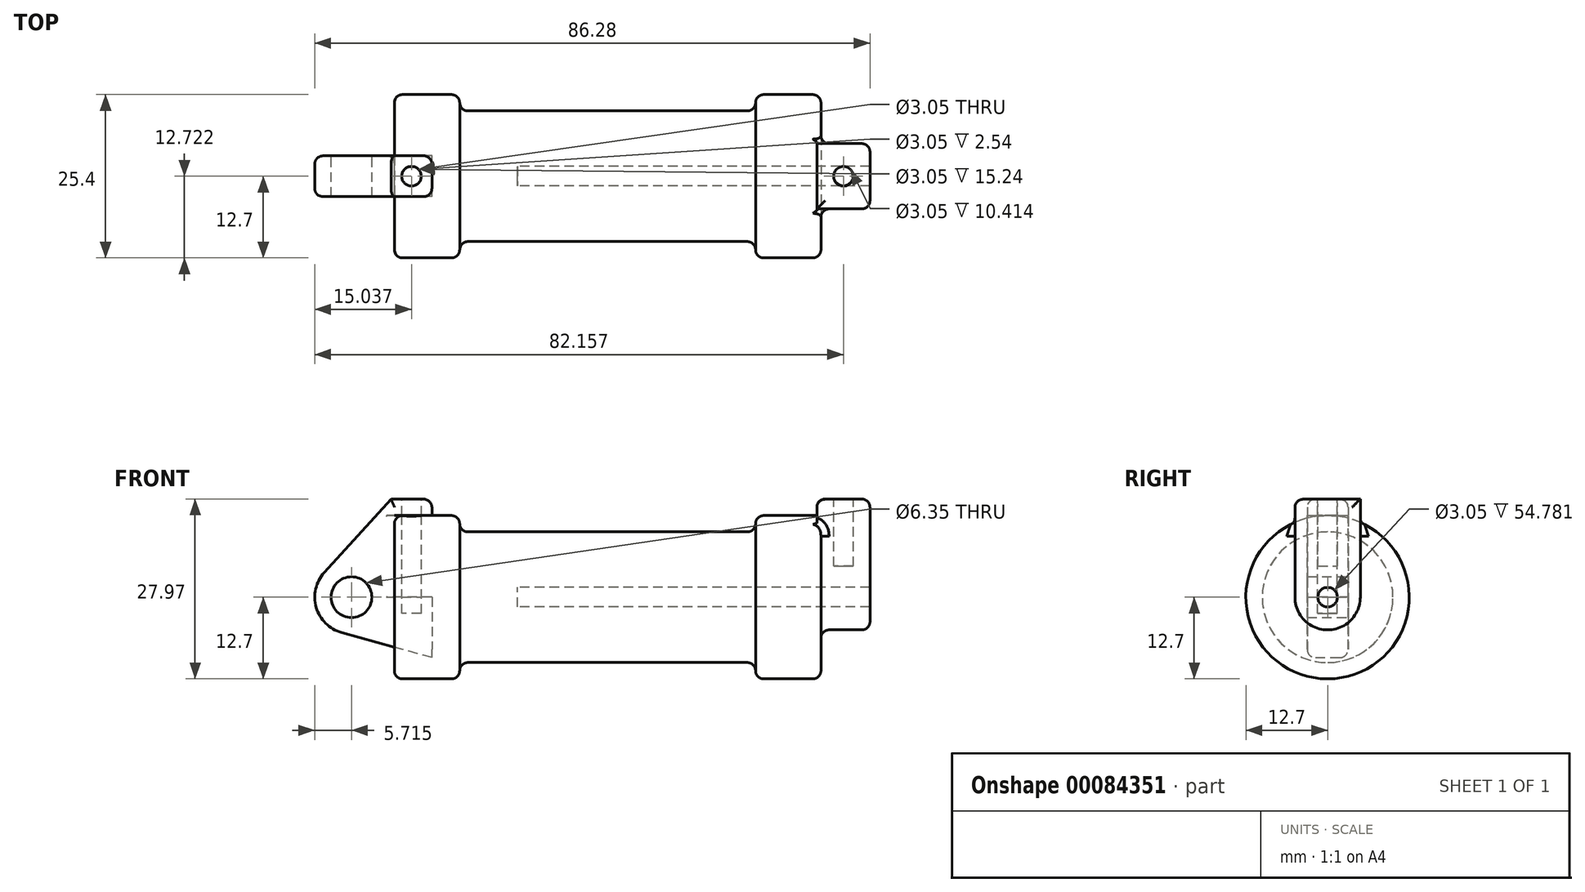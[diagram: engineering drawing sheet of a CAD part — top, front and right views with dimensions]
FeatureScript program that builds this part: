
annotation { "Feature Type Name" : "Feature", "Feature Type Description" : "" }
export const myFeature = defineFeature(function(context is Context, id is Id, definition is map)
    precondition{}
    {
        {
            var Q0;
            Q0=qCreatedBy(makeId("Front.planeOp"),FACE);
            var sketch = newSketch(context, id + "F0", { "sketchPlane" : qUnion([Q0])});
            skLineSegment(sketch, "E0", {"start": v(0, 0) * mm, "end": v(0, 12.7) * mm});
            skLineSegment(sketch, "E1", {"start": v(0, 12.7) * mm, "end": v(10.16, 12.7) * mm});
            skLineSegment(sketch, "E2", {"start": v(10.16, 12.7) * mm, "end": v(10.16, 10.16) * mm});
            skLineSegment(sketch, "E3", {"start": v(10.16, 10.16) * mm, "end": v(56.13, 10.16) * mm});
            skLineSegment(sketch, "E4", {"start": v(56.13, 10.16) * mm, "end": v(56.13, 12.7) * mm});
            skLineSegment(sketch, "E5", {"start": v(56.13, 12.7) * mm, "end": v(66.3, 12.7) * mm});
            skLineSegment(sketch, "E6", {"start": v(66.3, 12.7) * mm, "end": v(66.3, 0) * mm});
            skLineSegment(sketch, "E7", {"start": v(66.3, 0) * mm, "end": v(0, 0) * mm});
            skLineSegment(sketch, "E8", {"start": v(5.84, 15.24) * mm, "end": v(-0.5, 15.24) * mm});
            skLineSegment(sketch, "E9", {"start": v(-0.5, 15.24) * mm, "end": v(-10.88, 3.85) * mm});
            skLineSegment(sketch, "E10", {"start": v(0, 0) * mm, "end": v(-6.65, 0) * mm});
            skCircle(sketch, "E11", {"center": v(-6.65, 0) * mm, "radius": 5.72 * mm});
            skCircle(sketch, "E12", {"center": v(-6.65, 0) * mm, "radius": 3.18 * mm});
            skLineSegment(sketch, "E13", {"start": v(5.84, 15.24) * mm, "end": v(5.84, -9.4) * mm});
            skLineSegment(sketch, "E14", {"start": v(5.84, -9.4) * mm, "end": v(-8.18, -5.5) * mm});
            skSolve(sketch);
        }
        {
            var Q0;
            {var subQ0=sQuery(id+"F0.wireOp",EDGE,"E2");Q0=makeQuery(id+"F0.imprint","IMPRINT",FACE,{"disambiguationData":[TD([[makeQuery(id+"F0.imprint","IMPRINT",EDGE,{"derivedFrom":subQ0}),-1.0]])]});}
            var Q1;
            {var subQ0=sQuery(id+"F0.wireOp",EDGE,"E0");Q1=makeQuery(id+"F0.imprint","IMPRINT",FACE,{"disambiguationData":[TD([[makeQuery(id+"F0.imprint","IMPRINT",EDGE,{"derivedFrom":subQ0}),-1.0]])]});}
            var Q2;
            Q2=sQuery(id+"F0.wireOp",EDGE,"E7");
            revolve(context, id + "F1", {"entities" : qUnion([Q0, Q1]), "axis" : qUnion([Q2]), "revolveType" : RevolveType.FULL});
        }
        {
            var Q0;
            {var subQ3=sQuery(id+"F0.wireOp",EDGE,"E0");Q0=makeQuery(id+"F0.imprint","IMPRINT",FACE,{"disambiguationData":[TD([[makeQuery(id+"F0.imprint","IMPRINT",EDGE,{"derivedFrom":subQ3}),1.0]])]});}
            var Q1;
            {var subQ4=sQuery(id+"F0.wireOp",EDGE,"E12");Q1=makeQuery(id+"F0.imprint","IMPRINT",FACE,{"disambiguationData":[TD([[makeQuery(id+"F0.imprint","IMPRINT",EDGE,{"derivedFrom":subQ4}),-1.0]])]});}
            var Q2;
            {var subQ0=sQuery(id+"F0.wireOp",EDGE,"E14");Q2=makeQuery(id+"F0.imprint","IMPRINT",FACE,{"disambiguationData":[TD([[makeQuery(id+"F0.imprint","IMPRINT",EDGE,{"derivedFrom":subQ0}),-1.0]])]});}
            extrude(context, id + "F2", {"entities" : qUnion([Q0, Q1, Q2]), "endBound" : BoundingType.SYMMETRIC, "depth" : 6.35 * mm});
        }
        {
            var Q0;
            Q0=makeQuery(id+"F1.opRevolve","SWEPT_FACE",FACE,{"disambiguationData":[OSD([sQuery(id+"F0.wireOp",EDGE,"E6")])]});
            var sketch = newSketch(context, id + "F3", { "sketchPlane" : qUnion([Q0])});
            skCircle(sketch, "E15", {"center": v(0, 0) * mm, "radius": 1.52 * mm});
            skCircle(sketch, "E16", {"center": v(0, 0) * mm, "radius": 5.08 * mm});
            skLineSegment(sketch, "E17", {"start": v(-5.08, 0) * mm, "end": v(-5.08, 15.23) * mm});
            skLineSegment(sketch, "E18", {"start": v(5.08, 0.03) * mm, "end": v(5.08, 15.27) * mm});
            skLineSegment(sketch, "E19", {"start": v(-5.08, 15.23) * mm, "end": v(5.1, 15.27) * mm});
            skSolve(sketch);
        }
        {
            var Q0;
            {var subQ0=sQuery(id+"F3.wireOp",EDGE,"E17");var subQ1=sQuery(id+"F3.wireOp",EDGE,"E16");var subQ2=makeQuery(id+"F3.imprint","INTERSECT",VERTEX,{"derivedFrom":[subQ1,subQ0]});Q0=makeQuery(id+"F3.imprint","IMPRINT",FACE,{"disambiguationData":[TD([[makeQuery(id+"F3.imprint","IMPRINT",EDGE,{"disambiguationData":[TD([[subQ2,1.0]])],"derivedFrom":subQ1}),-1.0]])]});}
            var Q1;
            {var subQ0=sQuery(id+"F3.wireOp",EDGE,"E19");var subQ1=sQuery(id+"F3.wireOp",EDGE,"E17");var subQ2=makeQuery(id+"F3.imprint","INTERSECT",VERTEX,{"derivedFrom":[subQ1,subQ0]});Q1=makeQuery(id+"F3.imprint","IMPRINT",FACE,{"disambiguationData":[TD([[makeQuery(id+"F3.imprint","IMPRINT",EDGE,{"disambiguationData":[TD([[subQ2,-1.0]])],"derivedFrom":subQ0}),-1.0]])]});}
            var Q2;
            Q2=makeQuery(id+"F3.imprint","IMPRINT",FACE,{"disambiguationData":[TD([[makeQuery(id+"F3.imprint","IMPRINT",EDGE,{"derivedFrom":sQuery(id+"F3.wireOp",EDGE,"E15")}),-1.0]])]});
            extrude(context, id + "F4", {"entities" : qUnion([Q0, Q1, Q2]), "operationType" : NewBodyOperationType.ADD, "depth" : 7.62 * mm});
        }
        {
            var Q0;
            Q0=makeQuery(id+"F4.opExtrude","CAP_FACE",FACE,{"disambiguationData":[OSD([sQuery(id+"F3.wireOp",EDGE,"E15"),sQuery(id+"F3.wireOp",EDGE,"E16"),sQuery(id+"F3.wireOp",EDGE,"E17"),sQuery(id+"F3.wireOp",EDGE,"E18"),sQuery(id+"F3.wireOp",EDGE,"E19")])],"isStart":true});
            extrude(context, id + "F5", {"entities" : qUnion([Q0]), "operationType" : NewBodyOperationType.ADD, "endBound" : BoundingType.SYMMETRIC, "depth" : 1.27 * mm});
        }
        {
            var Q0;
            Q0=makeQuery(id+"F4.boolean.opBoolean","SPLIT",FACE,{"disambiguationData":[TD([makeQuery(id+"F4.opExtrude","SWEPT_FACE",FACE,{"disambiguationData":[OSD([sQuery(id+"F3.wireOp",EDGE,"E15")])]})])],"derivedFrom":makeQuery(id+"F1.opRevolve","SWEPT_FACE",FACE,{"disambiguationData":[OSD([sQuery(id+"F0.wireOp",EDGE,"E6")])]})});
            extrude(context, id + "F6", {"entities" : qUnion([Q0]), "operationType" : NewBodyOperationType.REMOVE, "oppositeDirection" : true, "depth" : 47.16 * mm});
        }
        {
            var Q0;
            {var subQ0=sQuery(id+"F3.wireOp",EDGE,"E19");Q0=makeQuery(id+"F5.boolean.opBoolean","MERGE",FACE,{"derivedFrom":[makeQuery(id+"F4.opExtrude","SWEPT_FACE",FACE,{"disambiguationData":[OSD([subQ0])]}),makeQuery(id+"F5.opExtrude","SWEPT_FACE",FACE,{"disambiguationData":[OSD([subQ0])]})]});}
            var sketch = newSketch(context, id + "F7", { "sketchPlane" : qUnion([Q0])});
            skCircle(sketch, "E20", {"center": v(69.79, 0.06) * mm, "radius": 1.52 * mm});
            skSolve(sketch);
        }
        {
            var Q0;
            Q0=makeQuery(id+"F2.opExtrude","SWEPT_FACE",FACE,{"disambiguationData":[OSD([sQuery(id+"F0.wireOp",EDGE,"E8")])]});
            var sketch = newSketch(context, id + "F8", { "sketchPlane" : qUnion([Q0])});
            skCircle(sketch, "E21", {"center": v(2.67, 0) * mm, "radius": 1.52 * mm});
            skSolve(sketch);
        }
        {
            var Q0;
            Q0=makeQuery(id+"F8.imprint","IMPRINT",FACE,{"disambiguationData":[TD([[makeQuery(id+"F8.imprint","IMPRINT",EDGE,{"derivedFrom":sQuery(id+"F8.wireOp",EDGE,"E21")}),1.0]])]});
            var Q1;
            Q1=sQuery(id+"F8.wireOp",EDGE,"E21");
            extrude(context, id + "F9", {"entities" : qUnion([Q0]), "operationType" : NewBodyOperationType.REMOVE, "surfaceEntities" : qUnion([Q1]), "oppositeDirection" : true, "depth" : 17.78 * mm});
        }
        {
            var Q0;
            Q0=makeQuery(id+"F7.imprint","IMPRINT",FACE,{"disambiguationData":[TD([[makeQuery(id+"F7.imprint","IMPRINT",EDGE,{"derivedFrom":sQuery(id+"F7.wireOp",EDGE,"E20")}),1.0]])]});
            var Q1;
            Q1=sQuery(id+"F7.wireOp",EDGE,"E20");
            extrude(context, id + "F10", {"entities" : qUnion([Q0]), "operationType" : NewBodyOperationType.REMOVE, "surfaceEntities" : qUnion([Q1]), "oppositeDirection" : true, "depth" : 10.4 * mm});
        }
        {
            var Q0;
            Q0=makeQuery(id+"F1.opRevolve","SWEPT_EDGE",EDGE,{"disambiguationData":[OSD([sQuery(id+"F0.wireOp",EDGE,"E1"),sQuery(id+"F0.wireOp",EDGE,"E2")])]});
            var Q1;
            Q1=makeQuery(id+"F1.opRevolve","SWEPT_EDGE",EDGE,{"disambiguationData":[OSD([sQuery(id+"F0.wireOp",EDGE,"E2"),sQuery(id+"F0.wireOp",EDGE,"E3")])]});
            var Q2;
            Q2=makeQuery(id+"F1.opRevolve","SWEPT_EDGE",EDGE,{"disambiguationData":[OSD([sQuery(id+"F0.wireOp",EDGE,"E4"),sQuery(id+"F0.wireOp",EDGE,"E5")])]});
            var Q3;
            Q3=makeQuery(id+"F1.opRevolve","SWEPT_EDGE",EDGE,{"disambiguationData":[OSD([sQuery(id+"F0.wireOp",EDGE,"E3"),sQuery(id+"F0.wireOp",EDGE,"E4")])]});
            var Q4;
            Q4=makeQuery(id+"F4.boolean.opBoolean","SPLIT",EDGE,{"disambiguationData":[OD(1.0)],"derivedFrom":makeQuery(id+"F1.opRevolve","SWEPT_EDGE",EDGE,{"disambiguationData":[OSD([sQuery(id+"F0.wireOp",EDGE,"E5"),sQuery(id+"F0.wireOp",EDGE,"E6")])]})});
            var Q5;
            Q5=makeQuery(id+"F1.opRevolve","SWEPT_EDGE",EDGE,{"disambiguationData":[OSD([sQuery(id+"F0.wireOp",EDGE,"E0"),sQuery(id+"F0.wireOp",EDGE,"E1")])]});
            fillet(context, id + "F11", {"entities" : qUnion([Q0, Q1, Q2, Q3, Q4, Q5]), "radius" : 1.27 * mm, "tangentPropagation" : true, "allowEdgeOverflow" : false});
        }
        {
            var Q0;
            Q0=makeQuery(id+"F2.opExtrude","CAP_EDGE",EDGE,{"disambiguationData":[OSD([sQuery(id+"F0.wireOp",EDGE,"E0")])],"isStart":true});
            var Q1;
            Q1=makeQuery(id+"F4.opExtrude","CAP_EDGE",EDGE,{"disambiguationData":[OSD([sQuery(id+"F3.wireOp",EDGE,"E17")])],"isStart":false});
            var Q2;
            Q2=makeQuery(id+"F4.opExtrude","CAP_EDGE",EDGE,{"disambiguationData":[OSD([sQuery(id+"F3.wireOp",EDGE,"E19")])],"isStart":false});
            var Q3;
            Q3=makeQuery(id+"F4.opExtrude","CAP_EDGE",EDGE,{"disambiguationData":[OSD([sQuery(id+"F3.wireOp",EDGE,"E16")])],"isStart":false});
            var Q4;
            Q4=makeQuery(id+"F4.opExtrude","CAP_EDGE",EDGE,{"disambiguationData":[OSD([sQuery(id+"F3.wireOp",EDGE,"E18")])],"isStart":false});
            var Q5;
            Q5=makeQuery(id+"F4.opExtrude","CAP_EDGE",EDGE,{"disambiguationData":[OSD([sQuery(id+"F3.wireOp",EDGE,"E16")])],"isStart":true});
            var Q6;
            {var subQ0=sQuery(id+"F3.wireOp",EDGE,"E16");var subQ1=sQuery(id+"F3.wireOp",EDGE,"E18");Q6=makeQuery(id+"F4.boolean.opBoolean","SPLIT",EDGE,{"disambiguationData":[TD([makeQuery(id+"F4.opExtrude","SWEPT_FACE",FACE,{"disambiguationData":[OSD([subQ0])]})])],"derivedFrom":makeQuery(id+"F4.opExtrude","CAP_EDGE",EDGE,{"disambiguationData":[OSD([subQ1])],"isStart":true})});}
            var Q7;
            {var subQ0=sQuery(id+"F3.wireOp",EDGE,"E19");var subQ1=sQuery(id+"F3.wireOp",EDGE,"E18");Q7=makeQuery(id+"F5.boolean.opBoolean","MERGE",EDGE,{"derivedFrom":[makeQuery(id+"F4.opExtrude","SWEPT_EDGE",EDGE,{"disambiguationData":[OSD([subQ1,subQ0])]}),makeQuery(id+"F5.opExtrude","SWEPT_EDGE",EDGE,{"disambiguationData":[OSD([subQ1,subQ0])]})]});}
            var Q8;
            {var subQ0=sQuery(id+"F3.wireOp",EDGE,"E16");var subQ1=sQuery(id+"F3.wireOp",EDGE,"E17");Q8=makeQuery(id+"F4.boolean.opBoolean","SPLIT",EDGE,{"disambiguationData":[TD([makeQuery(id+"F4.opExtrude","SWEPT_FACE",FACE,{"disambiguationData":[OSD([subQ0])]})])],"derivedFrom":makeQuery(id+"F4.opExtrude","CAP_EDGE",EDGE,{"disambiguationData":[OSD([subQ1])],"isStart":true})});}
            var Q9;
            Q9=makeQuery(id+"F5.opExtrude","CAP_EDGE",EDGE,{"disambiguationData":[OSD([sQuery(id+"F3.wireOp",EDGE,"E19")])],"isStart":false});
            var Q10;
            {var subQ0=sQuery(id+"F3.wireOp",EDGE,"E17");Q10=makeQuery(id+"F11.opFillet","BLEND_EDGE",EDGE,{"blendedFrom":[makeQuery(id+"F4.boolean.opBoolean","SPLIT",EDGE,{"disambiguationData":[OD(1.0)],"derivedFrom":makeQuery(id+"F1.opRevolve","SWEPT_EDGE",EDGE,{"disambiguationData":[OSD([sQuery(id+"F0.wireOp",EDGE,"E5"),sQuery(id+"F0.wireOp",EDGE,"E6")])]})}),makeQuery(id+"F5.boolean.opBoolean","MERGE",FACE,{"derivedFrom":[makeQuery(id+"F4.opExtrude","SWEPT_FACE",FACE,{"disambiguationData":[OSD([subQ0])]}),makeQuery(id+"F5.opExtrude","SWEPT_FACE",FACE,{"disambiguationData":[OSD([subQ0])]})]})],"blendedInto":[makeQuery(id+"F5.boolean.opBoolean","MERGE",FACE,{"derivedFrom":[makeQuery(id+"F4.opExtrude","SWEPT_FACE",FACE,{"disambiguationData":[OSD([subQ0])]}),makeQuery(id+"F5.opExtrude","SWEPT_FACE",FACE,{"disambiguationData":[OSD([subQ0])]})]})]});}
            var Q11;
            {var subQ0=sQuery(id+"F3.wireOp",EDGE,"E18");Q11=makeQuery(id+"F11.opFillet","BLEND_EDGE",EDGE,{"blendedFrom":[makeQuery(id+"F4.boolean.opBoolean","SPLIT",EDGE,{"disambiguationData":[OD(1.0)],"derivedFrom":makeQuery(id+"F1.opRevolve","SWEPT_EDGE",EDGE,{"disambiguationData":[OSD([sQuery(id+"F0.wireOp",EDGE,"E5"),sQuery(id+"F0.wireOp",EDGE,"E6")])]})}),makeQuery(id+"F5.boolean.opBoolean","MERGE",FACE,{"derivedFrom":[makeQuery(id+"F4.opExtrude","SWEPT_FACE",FACE,{"disambiguationData":[OSD([subQ0])]}),makeQuery(id+"F5.opExtrude","SWEPT_FACE",FACE,{"disambiguationData":[OSD([subQ0])]})]})],"blendedInto":[makeQuery(id+"F5.boolean.opBoolean","MERGE",FACE,{"derivedFrom":[makeQuery(id+"F4.opExtrude","SWEPT_FACE",FACE,{"disambiguationData":[OSD([subQ0])]}),makeQuery(id+"F5.opExtrude","SWEPT_FACE",FACE,{"disambiguationData":[OSD([subQ0])]})]})]});}
            var Q12;
            {var subQ0=sQuery(id+"F3.wireOp",EDGE,"E19");var subQ1=sQuery(id+"F3.wireOp",EDGE,"E17");Q12=makeQuery(id+"F5.boolean.opBoolean","MERGE",EDGE,{"derivedFrom":[makeQuery(id+"F4.opExtrude","SWEPT_EDGE",EDGE,{"disambiguationData":[OSD([subQ1,subQ0])]}),makeQuery(id+"F5.opExtrude","SWEPT_EDGE",EDGE,{"disambiguationData":[OSD([subQ1,subQ0])]})]});}
            var Q13;
            Q13=makeQuery(id+"F5.opExtrude","CAP_EDGE",EDGE,{"disambiguationData":[OSD([sQuery(id+"F0.wireOp",EDGE,"E5"),sQuery(id+"F0.wireOp",EDGE,"E6")])],"isStart":false});
            var Q14;
            Q14=makeQuery(id+"F2.opExtrude","CAP_EDGE",EDGE,{"disambiguationData":[OSD([sQuery(id+"F0.wireOp",EDGE,"E9")])],"isStart":false});
            var Q15;
            Q15=makeQuery(id+"F2.opExtrude","CAP_EDGE",EDGE,{"disambiguationData":[OSD([sQuery(id+"F0.wireOp",EDGE,"E8")])],"isStart":false});
            var Q16;
            Q16=makeQuery(id+"F2.opExtrude","CAP_EDGE",EDGE,{"disambiguationData":[OSD([sQuery(id+"F0.wireOp",EDGE,"E11")])],"isStart":false});
            var Q17;
            Q17=makeQuery(id+"F2.opExtrude","CAP_EDGE",EDGE,{"disambiguationData":[OSD([sQuery(id+"F0.wireOp",EDGE,"E14")])],"isStart":false});
            var Q18;
            {var subQ0=sQuery(id+"F0.wireOp",EDGE,"E13");Q18=makeQuery(id+"F2.opExtrude","CAP_EDGE",EDGE,{"disambiguationData":[OSD([subQ0]),TDD([makeQuery(id+"F0.imprint","IMPRINT",EDGE,{"disambiguationData":[TD([[makeQuery(id+"F0.imprint","INTERSECT",VERTEX,{"derivedFrom":[sQuery(id+"F0.wireOp",EDGE,"E8"),subQ0]}),-1.0]])],"derivedFrom":subQ0})])],"isStart":false});}
            var Q19;
            Q19=makeQuery(id+"F2.opExtrude","CAP_EDGE",EDGE,{"disambiguationData":[OSD([sQuery(id+"F0.wireOp",EDGE,"E11")])],"isStart":true});
            var Q20;
            Q20=makeQuery(id+"F2.opExtrude","CAP_EDGE",EDGE,{"disambiguationData":[OSD([sQuery(id+"F0.wireOp",EDGE,"E8")])],"isStart":true});
            var Q21;
            Q21=makeQuery(id+"F2.opExtrude","SWEPT_EDGE",EDGE,{"disambiguationData":[OSD([sQuery(id+"F0.wireOp",EDGE,"E8"),sQuery(id+"F0.wireOp",EDGE,"E13")])]});
            var Q22;
            {var subQ0=sQuery(id+"F0.wireOp",EDGE,"E13");Q22=makeQuery(id+"F2.opExtrude","CAP_EDGE",EDGE,{"disambiguationData":[OSD([subQ0]),TDD([makeQuery(id+"F0.imprint","IMPRINT",EDGE,{"disambiguationData":[TD([[makeQuery(id+"F0.imprint","INTERSECT",VERTEX,{"derivedFrom":[sQuery(id+"F0.wireOp",EDGE,"E8"),subQ0]}),-1.0]])],"derivedFrom":subQ0})])],"isStart":true});}
            var Q23;
            Q23=makeQuery(id+"F2.opExtrude","CAP_EDGE",EDGE,{"disambiguationData":[OSD([sQuery(id+"F0.wireOp",EDGE,"E9")])],"isStart":true});
            var Q24;
            Q24=makeQuery(id+"F2.opExtrude","CAP_EDGE",EDGE,{"disambiguationData":[OSD([sQuery(id+"F0.wireOp",EDGE,"E14")])],"isStart":true});
            fillet(context, id + "F12", {"entities" : qUnion([Q0, Q1, Q2, Q3, Q4, Q5, Q6, Q7, Q8, Q9, Q10, Q11, Q12, Q13, Q14, Q15, Q16, Q17, Q18, Q19, Q20, Q21, Q22, Q23, Q24]), "radius" : 1.27 * mm, "tangentPropagation" : true, "allowEdgeOverflow" : false});
        }
    });
